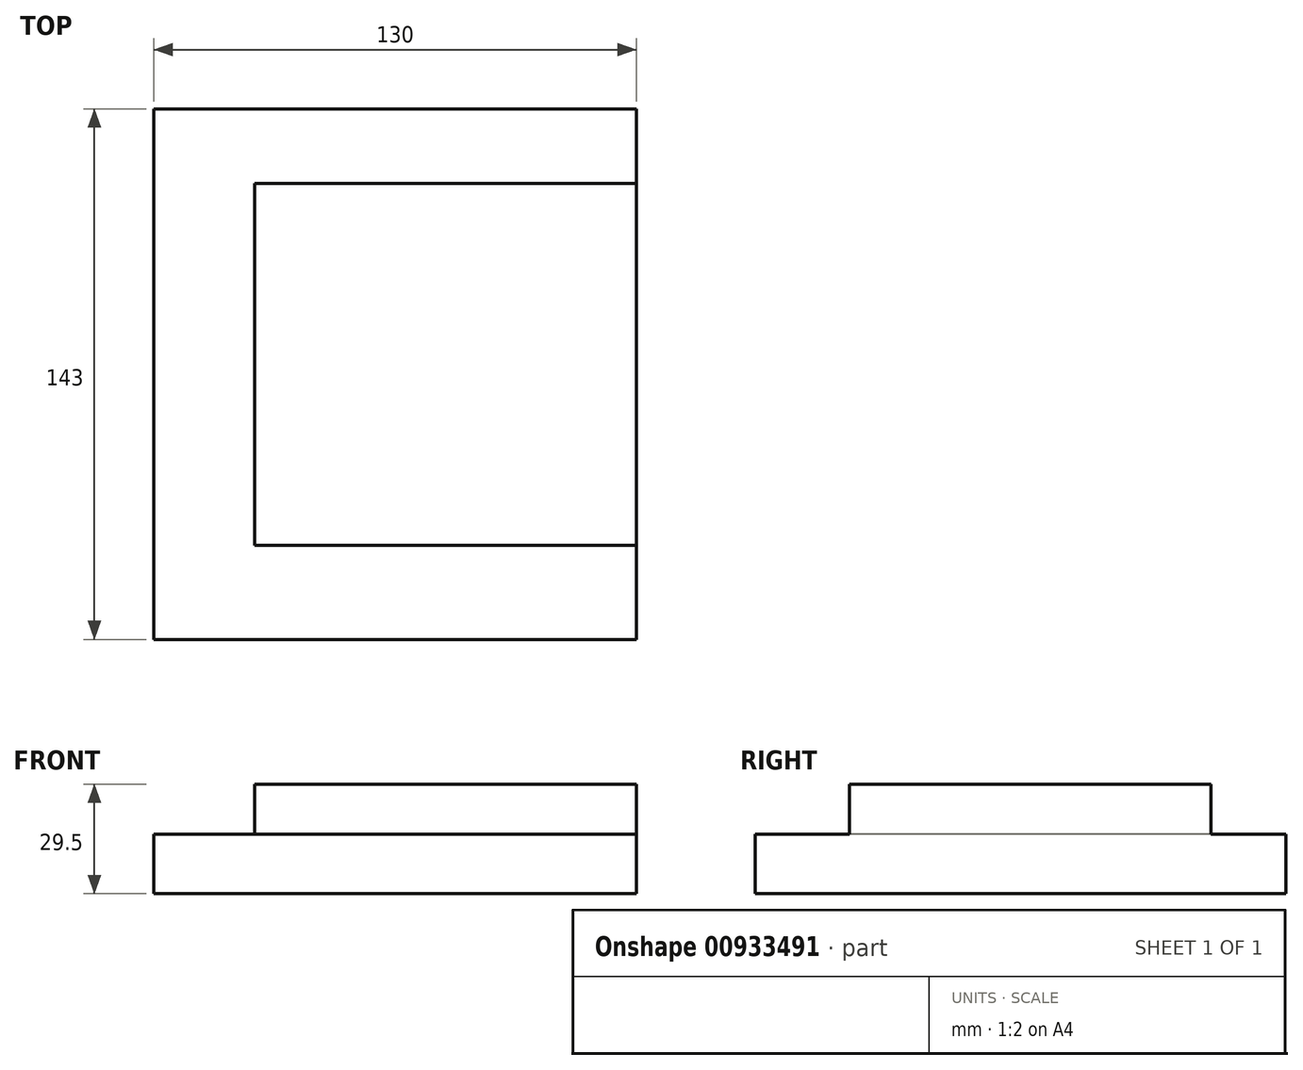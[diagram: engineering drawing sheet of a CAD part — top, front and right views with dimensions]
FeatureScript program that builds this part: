
annotation { "Feature Type Name" : "Feature", "Feature Type Description" : "" }
export const myFeature = defineFeature(function(context is Context, id is Id, definition is map)
    precondition{}
    {
        {
            var Q0;
            Q0=qCreatedBy(makeId("Top.planeOp"),FACE);
            var sketch = newSketch(context, id + "F0", { "sketchPlane" : qUnion([Q0])});
            skLineSegment(sketch, "E0.bottom", {"start": v(65, 71.5) * mm, "end": v(-65, 71.5) * mm});
            skLineSegment(sketch, "E0.top", {"start": v(65, -71.5) * mm, "end": v(-65, -71.5) * mm});
            skLineSegment(sketch, "E0.left", {"start": v(65, 71.5) * mm, "end": v(65, -71.5) * mm});
            skLineSegment(sketch, "E0.right", {"start": v(-65, 71.5) * mm, "end": v(-65, -71.5) * mm});
            skPoint(sketch, "E0.middle", {"position": v(0, 0) * mm});
            skSolve(sketch);
        }
        {
            var Q0;
            Q0=makeQuery(id+"F0.imprint","IMPRINT",FACE,{"disambiguationData":[TD([[makeQuery(id+"F0.imprint","IMPRINT",EDGE,{"derivedFrom":sQuery(id+"F0.wireOp",EDGE,"E0.bottom")}),1.0]])]});
            extrude(context, id + "F1", {"entities" : qUnion([Q0]), "depth" : 29.5 * mm, "offsetDistance" : 25.4 * mm});
        }
        {
            var Q0;
            Q0=makeQuery(id+"F1.opExtrude","CAP_FACE",FACE,{"disambiguationData":[OSD([sQuery(id+"F0.wireOp",EDGE,"E0.bottom"),sQuery(id+"F0.wireOp",EDGE,"E0.top"),sQuery(id+"F0.wireOp",EDGE,"E0.left"),sQuery(id+"F0.wireOp",EDGE,"E0.right")])],"isStart":false});
            var sketch = newSketch(context, id + "F2", { "sketchPlane" : qUnion([Q0])});
            skLineSegment(sketch, "E1", {"start": v(65, 0) * mm, "end": v(0, 71.5) * mm, "construction": true});
            skLineSegment(sketch, "E2", {"start": v(0, 71.5) * mm, "end": v(32.5, 35.75) * mm, "construction": true});
            skLineSegment(sketch, "E3", {"start": v(32.5, 35.75) * mm, "end": v(65, 71.5) * mm, "construction": true});
            skLineSegment(sketch, "E4", {"start": v(65, 51.37) * mm, "end": v(-37.85, 51.37) * mm});
            skLineSegment(sketch, "E5", {"start": v(-37.85, 51.37) * mm, "end": v(-37.85, -46.1) * mm});
            skLineSegment(sketch, "E6", {"start": v(-37.85, -46.1) * mm, "end": v(65, -46.1) * mm});
            skLineSegment(sketch, "E7", {"start": v(65, -46.1) * mm, "end": v(65, -71.5) * mm});
            skLineSegment(sketch, "E8", {"start": v(65, -71.5) * mm, "end": v(-65, -71.5) * mm});
            skLineSegment(sketch, "E9", {"start": v(-65, -71.5) * mm, "end": v(-65, 71.5) * mm});
            skLineSegment(sketch, "E10", {"start": v(-65, 71.5) * mm, "end": v(65, 71.5) * mm});
            skSolve(sketch);
        }
        {
            var Q0;
            Q0 = qSketchRegion(id + "F2", true);
            var Q1;
            {var subQ0=sQuery(id+"F2.wireOp",EDGE,"E4");Q1=makeQuery(id+"F2.imprint","IMPRINT",FACE,{"disambiguationData":[TD([[makeQuery(id+"F2.imprint","IMPRINT",EDGE,{"derivedFrom":subQ0}),-1.0]])]});}
            extrude(context, id + "F3", {"entities" : qUnion([Q0, Q1]), "operationType" : NewBodyOperationType.REMOVE, "oppositeDirection" : true, "depth" : 13.5 * mm, "offsetDistance" : 25.4 * mm});
        }
    });
